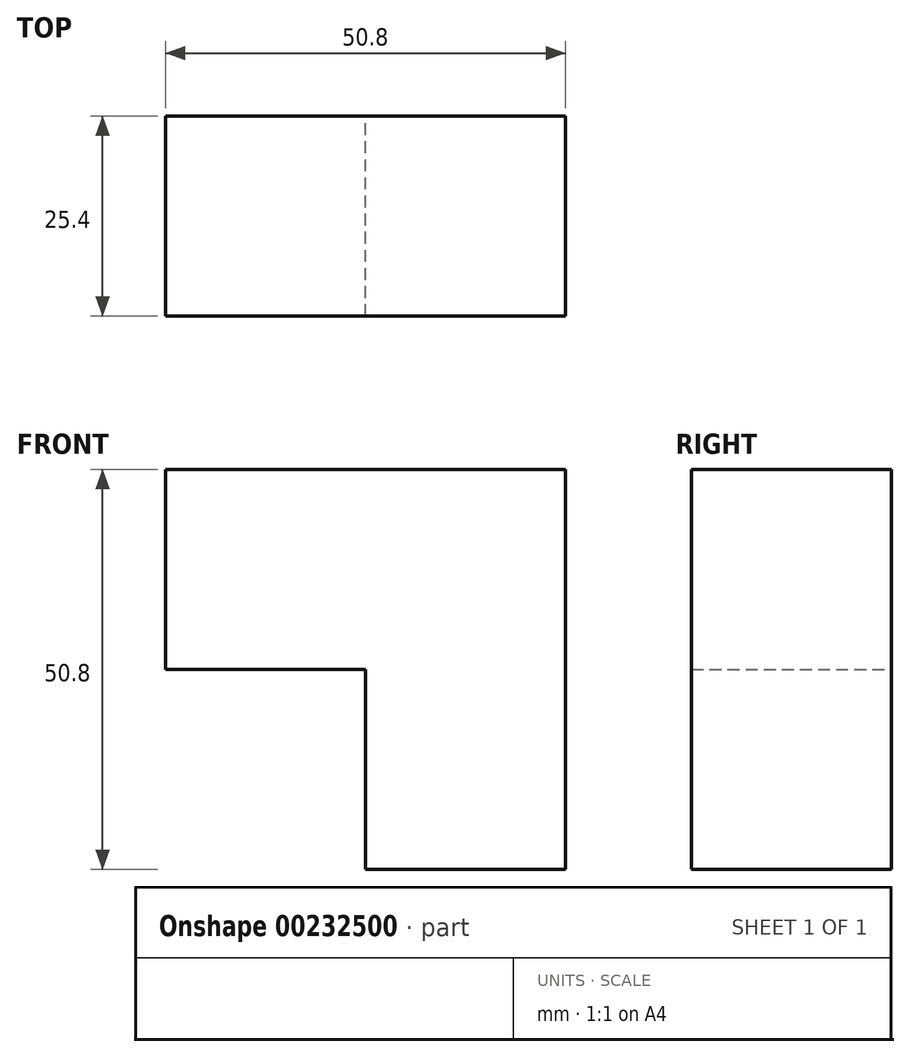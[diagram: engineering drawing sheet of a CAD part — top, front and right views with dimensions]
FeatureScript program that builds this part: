
annotation { "Feature Type Name" : "Feature", "Feature Type Description" : "" }
export const myFeature = defineFeature(function(context is Context, id is Id, definition is map)
    precondition{}
    {
        {
            var Q0;
            Q0=qCreatedBy(makeId("Front.planeOp"),FACE);
            var sketch = newSketch(context, id + "F0", { "sketchPlane" : qUnion([Q0])});
            skLineSegment(sketch, "E0", {"start": v(-25.4, 0) * mm, "end": v(0, 0) * mm});
            skLineSegment(sketch, "E1", {"start": v(-25.4, 25.4) * mm, "end": v(-25.4, 0) * mm});
            skLineSegment(sketch, "E2", {"start": v(-25.4, 25.4) * mm, "end": v(0, 25.4) * mm});
            skLineSegment(sketch, "E3", {"start": v(0, 25.4) * mm, "end": v(25.4, 25.4) * mm});
            skLineSegment(sketch, "E4", {"start": v(25.4, 25.4) * mm, "end": v(25.4, -25.4) * mm});
            skLineSegment(sketch, "E5", {"start": v(0, 0) * mm, "end": v(0, -25.4) * mm});
            skLineSegment(sketch, "E6", {"start": v(25.4, -25.4) * mm, "end": v(0, -25.4) * mm});
            skSolve(sketch);
        }
        {
            var Q0;
            Q0=makeQuery(id+"F0.imprint","IMPRINT",FACE,{"disambiguationData":[TD([[makeQuery(id+"F0.imprint","IMPRINT",EDGE,{"derivedFrom":sQuery(id+"F0.wireOp",EDGE,"E0")}),1.0]])]});
            extrude(context, id + "F1", {"entities" : qUnion([Q0]), "depth" : 25.4 * mm});
        }
    });
